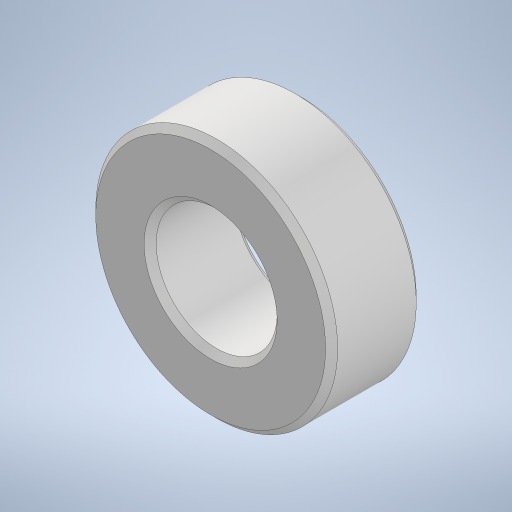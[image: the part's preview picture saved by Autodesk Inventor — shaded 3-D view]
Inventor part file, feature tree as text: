
AUTODESK INVENTOR PART (.ipt)
format: ipt  version: 2024 (Build 280153000, 153)  size: 244,736 bytes
history: native  units: mm
features: extrude x1, chamfer x1, sketch x1
ambient origin geometry x8: Origin, YZ Plane, XZ Plane, XY Plane, X Axis, Y Axis, Z Axis, Center Point
bodies: Solid1 (feature_tree)
feature tree (3):
  extrude  "Extrusion1"  Depth=4.0mm
  chamfer  "Chamfer1"  Distance=3.0mm
  sketch  "Sketch1"  dims[d0=8.0mm d1=4.0mm d2=3.0mm d3=0.0mm d4=0.2mm d5=2.0mm d6=45.0deg]
